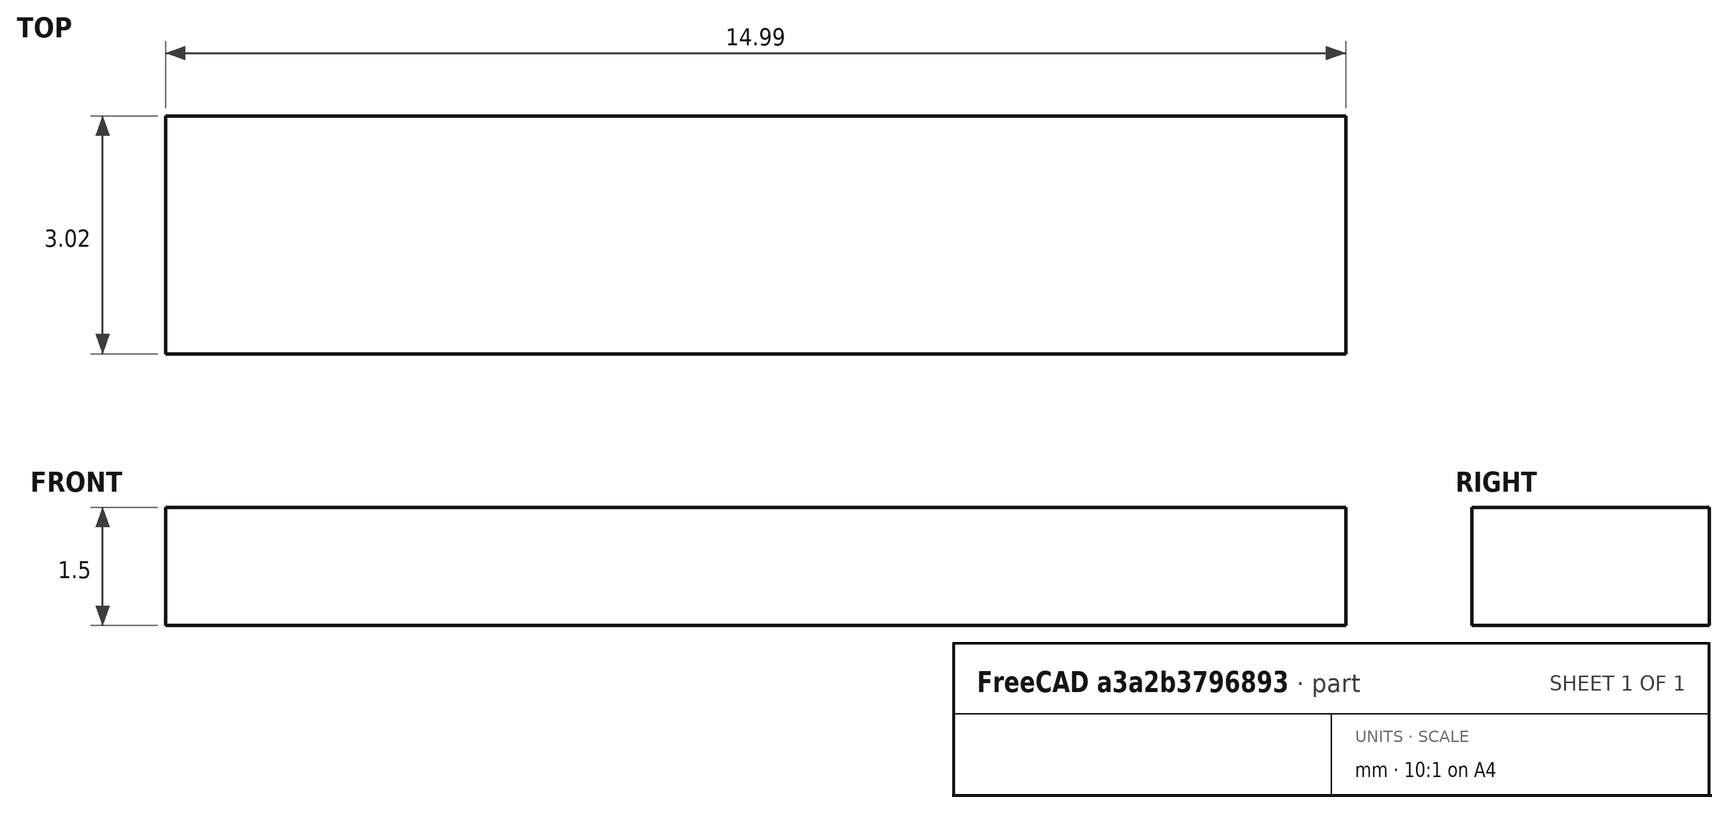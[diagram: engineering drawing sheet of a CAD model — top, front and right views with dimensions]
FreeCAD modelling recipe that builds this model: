
FCSTD DOCUMENT  (FreeCAD 0.19R24291 (Git))
Label: 1mmX10WireHarnis
License: All rights reserved
LicenseURL: http://en.wikipedia.org/wiki/All_rights_reserved
objects: Sketcher::SketchObject×1, PartDesign::Pad×1, PartDesign::Body×1
note: 4 computed .brp shape members not serialized (recipe doc carries the construction recipe); baked Part::Feature solids carry a one-line shape summary decoded from their .brp

FEATURE [Sketcher::SketchObject] Sketch
  FullyConstrained = false
  MapMode = 5
  Support = -> [XY_Plane]
  sketch-geometry (4):
    g0: LineSegment StartX=0 StartY=0 StartZ=0 EndX=14.9899 EndY=0 EndZ=0
    g1: LineSegment StartX=14.9899 StartY=0 StartZ=0 EndX=14.9899 EndY=3.02225 EndZ=0
    g2: LineSegment StartX=14.9899 StartY=3.02225 StartZ=0 EndX=0 EndY=3.02225 EndZ=0
    g3: LineSegment StartX=0 StartY=3.02225 StartZ=0 EndX=0 EndY=0 EndZ=0
  constraints (9):
    c: Coincident(g0,g1)
    c: Coincident(g1,g2)
    c: Coincident(g2,g3)
    c: Coincident(g3,g0)
    c: Horizontal(g0)
    c: Horizontal(g2)
    c: Vertical(g1)
    c: Vertical(g3)
    c: Coincident(g0,g-1)
FEATURE [PartDesign::Pad] Pad
  Direction = (1,1,1)
  Length = 1.5
  Length2 = 100
  Profile = -> Sketch
  Type = 0
FEATURE [PartDesign::Body] Body
  Group = -> [Sketch,Pad]
  Origin = -> Origin
  Tip = -> Pad
